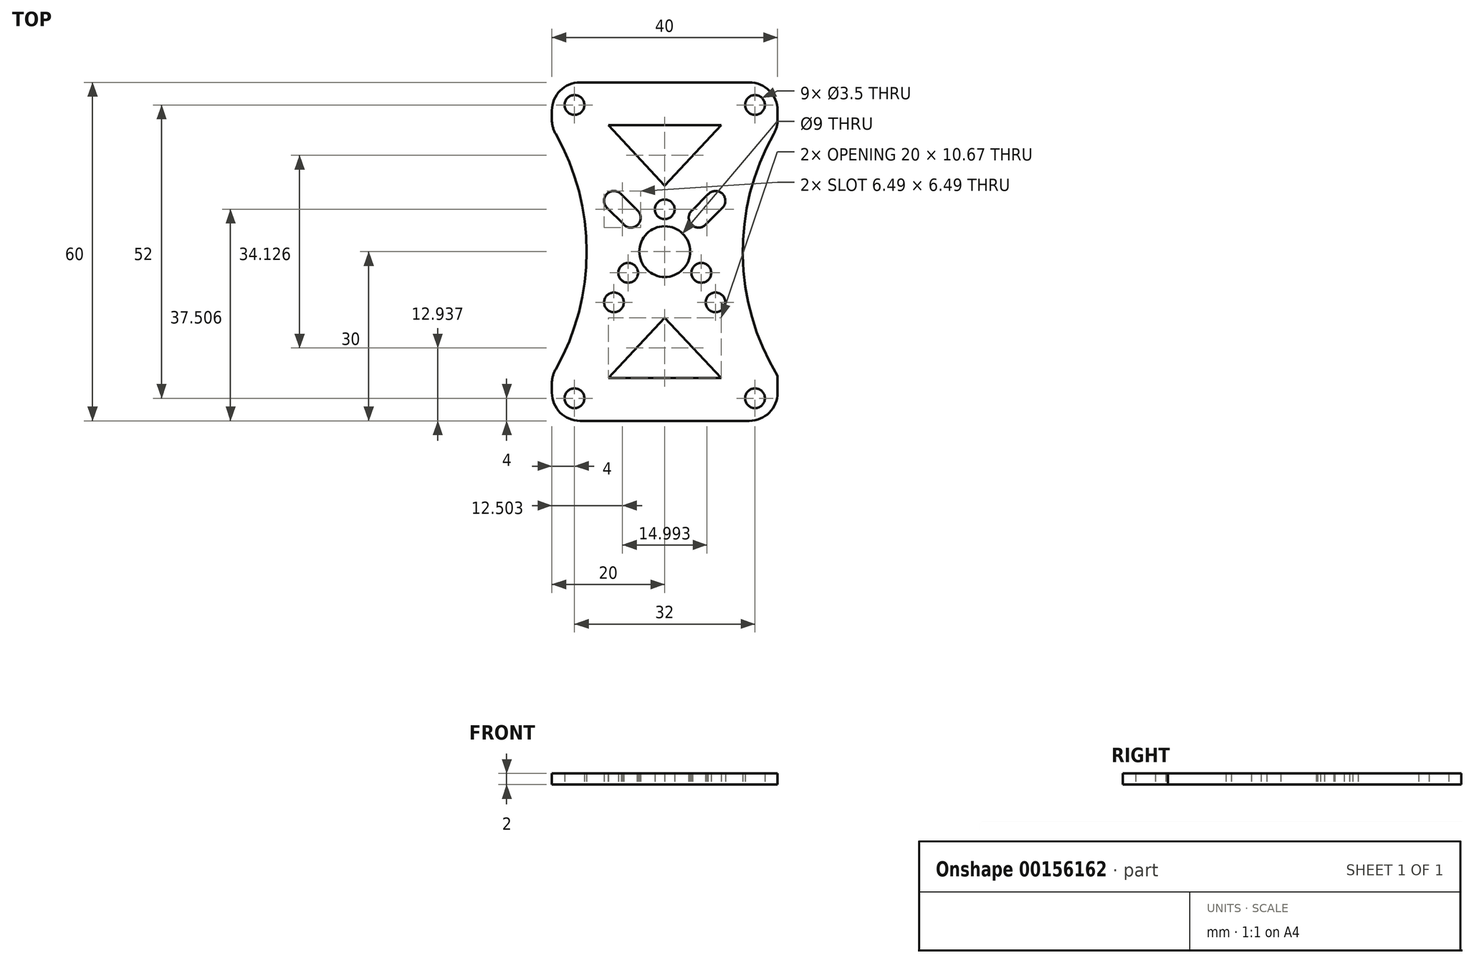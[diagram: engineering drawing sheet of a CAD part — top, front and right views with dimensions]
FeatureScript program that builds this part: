
annotation { "Feature Type Name" : "Feature", "Feature Type Description" : "" }
export const myFeature = defineFeature(function(context is Context, id is Id, definition is map)
    precondition{}
    {
        {
            var Q0;
            Q0=qCreatedBy(makeId("Top.planeOp"),FACE);
            var sketch = newSketch(context, id + "F0", { "sketchPlane" : qUnion([Q0])});
            skLineSegment(sketch, "E0.bottom", {"start": v(-20, 30) * mm, "end": v(20, 30) * mm});
            skLineSegment(sketch, "E0.top", {"start": v(-20, -30) * mm, "end": v(20, -30) * mm});
            skLineSegment(sketch, "E0.left", {"start": v(-20, 30) * mm, "end": v(-20, -30) * mm});
            skLineSegment(sketch, "E0.right", {"start": v(20, 30) * mm, "end": v(20, -30) * mm});
            skPoint(sketch, "E0.middle", {"position": v(0, 0) * mm});
            skCircle(sketch, "E1", {"center": v(-16, 26) * mm, "radius": 1.75 * mm});
            skCircle(sketch, "E2", {"center": v(-9, 9) * mm, "radius": 1.75 * mm});
            skCircle(sketch, "E3", {"center": v(-6, 6) * mm, "radius": 1.75 * mm});
            skLineSegment(sketch, "E4", {"start": v(-7.84, 10.31) * mm, "end": v(-4.92, 7.38) * mm});
            skLineSegment(sketch, "E5", {"start": v(-10.4, 7.95) * mm, "end": v(-6.95, 4.53) * mm});
            skCircle(sketch, "E6.MirrorC", {"center": v(9, 9) * mm, "radius": 1.75 * mm});
            skLineSegment(sketch, "E7.MirrorCS", {"start": v(7.84, 10.31) * mm, "end": v(4.92, 7.38) * mm});
            skLineSegment(sketch, "E8.MirrorCS", {"start": v(10.4, 7.95) * mm, "end": v(6.95, 4.53) * mm});
            skCircle(sketch, "E9.MirrorC", {"center": v(6, 6) * mm, "radius": 1.75 * mm});
            skCircle(sketch, "E10.MirrorC", {"center": v(16, 26) * mm, "radius": 1.75 * mm});
            skCircle(sketch, "E11.MirrorC", {"center": v(-16, -26) * mm, "radius": 1.75 * mm});
            skCircle(sketch, "E12.MirrorC", {"center": v(16, -26) * mm, "radius": 1.75 * mm});
            skCircle(sketch, "E13.MirrorC", {"center": v(-9, -9) * mm, "radius": 1.75 * mm});
            skCircle(sketch, "E14.MirrorC", {"center": v(9, -9) * mm, "radius": 1.75 * mm});
            skLineSegment(sketch, "E15", {"start": v(0, -22.4) * mm, "end": v(10, -22.4) * mm});
            skLineSegment(sketch, "E16", {"start": v(10, -22.4) * mm, "end": v(0, -11.73) * mm});
            skLineSegment(sketch, "E17.MirrorCS", {"start": v(-10, -22.4) * mm, "end": v(0, -11.73) * mm});
            skLineSegment(sketch, "E18.MirrorCS", {"start": v(0, -22.4) * mm, "end": v(-10, -22.4) * mm});
            skLineSegment(sketch, "E19.MirrorCS", {"start": v(10, 22.4) * mm, "end": v(0, 11.73) * mm});
            skLineSegment(sketch, "E20.MirrorCS", {"start": v(-10, 22.4) * mm, "end": v(0, 11.73) * mm});
            skLineSegment(sketch, "E21.MirrorCS", {"start": v(0, 22.4) * mm, "end": v(10, 22.4) * mm});
            skLineSegment(sketch, "E22.MirrorCS", {"start": v(0, 22.4) * mm, "end": v(-10, 22.4) * mm});
            skArc(sketch, "E23", {"start": v(-20, -22) * mm, "mid": v(-13.83, 0) * mm, "end": v(-20, 22) * mm});
            skArc(sketch, "E24.MirrorCS", {"start": v(20, -22) * mm, "mid": v(13.83, 0) * mm, "end": v(20, 22) * mm});
            skCircle(sketch, "E25", {"center": v(0, 0) * mm, "radius": 4.5 * mm});
            skCircle(sketch, "E26", {"center": v(0, 0) * mm, "radius": 7.5 * mm, "construction": true});
            skCircle(sketch, "E27", {"center": v(0, 7.5) * mm, "radius": 1.75 * mm});
            skCircle(sketch, "E28", {"center": v(6.49, -3.77) * mm, "radius": 1.75 * mm});
            skCircle(sketch, "E29.MirrorC", {"center": v(-6.49, -3.77) * mm, "radius": 1.75 * mm});
            skSolve(sketch);
        }
        {
            var Q0;
            {var subQ27=sQuery(id+"F0.wireOp",EDGE,"E0.bottom");Q0=makeQuery(id+"F0.imprint","IMPRINT",FACE,{"disambiguationData":[TD([[makeQuery(id+"F0.imprint","IMPRINT",EDGE,{"derivedFrom":subQ27}),-1.0]])]});}
            extrude(context, id + "F1", {"entities" : qUnion([Q0]), "depth" : 2 * mm});
        }
        {
            var Q0;
            Q0=makeQuery(id+"F1.opExtrude","SWEPT_EDGE",EDGE,{"disambiguationData":[OSD([sQuery(id+"F0.wireOp",EDGE,"E0.bottom"),sQuery(id+"F0.wireOp",EDGE,"E0.left")])]});
            var Q1;
            Q1=makeQuery(id+"F1.opExtrude","SWEPT_EDGE",EDGE,{"disambiguationData":[OSD([sQuery(id+"F0.wireOp",EDGE,"E0.top"),sQuery(id+"F0.wireOp",EDGE,"E0.left")])]});
            var Q2;
            Q2=makeQuery(id+"F1.opExtrude","SWEPT_EDGE",EDGE,{"disambiguationData":[OSD([sQuery(id+"F0.wireOp",EDGE,"E0.top"),sQuery(id+"F0.wireOp",EDGE,"E0.right")])]});
            var Q3;
            Q3=makeQuery(id+"F1.opExtrude","SWEPT_EDGE",EDGE,{"disambiguationData":[OSD([sQuery(id+"F0.wireOp",EDGE,"E0.bottom"),sQuery(id+"F0.wireOp",EDGE,"E0.right")])]});
            var Q4;
            {var subQ0=sQuery(id+"F0.wireOp",EDGE,"E24.MirrorCS");var subQ1=sQuery(id+"F0.wireOp",EDGE,"E0.right");Q4=makeQuery(id+"F1.opExtrude","SWEPT_EDGE",EDGE,{"disambiguationData":[OSD([subQ1,subQ0]),TDD([makeQuery(id+"F0.imprint","INTERSECT",VERTEX,{"disambiguationData":[OD(0.0)],"derivedFrom":[subQ1,subQ0]})])]});}
            var Q5;
            {var subQ0=sQuery(id+"F0.wireOp",EDGE,"E23");var subQ1=sQuery(id+"F0.wireOp",EDGE,"E0.left");Q5=makeQuery(id+"F1.opExtrude","SWEPT_EDGE",EDGE,{"disambiguationData":[OSD([subQ1,subQ0]),TDD([makeQuery(id+"F0.imprint","INTERSECT",VERTEX,{"disambiguationData":[OD(0.0)],"derivedFrom":[subQ1,subQ0]})])]});}
            var Q6;
            {var subQ0=sQuery(id+"F0.wireOp",EDGE,"E23");var subQ1=sQuery(id+"F0.wireOp",EDGE,"E0.left");Q6=makeQuery(id+"F1.opExtrude","SWEPT_EDGE",EDGE,{"disambiguationData":[OSD([subQ1,subQ0]),TDD([makeQuery(id+"F0.imprint","INTERSECT",VERTEX,{"disambiguationData":[OD(1.0)],"derivedFrom":[subQ1,subQ0]})])]});}
            fillet(context, id + "F2", {"entities" : qUnion([Q0, Q1, Q2, Q3, Q4, Q5, Q6]), "radius" : 5 * mm, "tangentPropagation" : true, "allowEdgeOverflow" : false});
        }
    });
